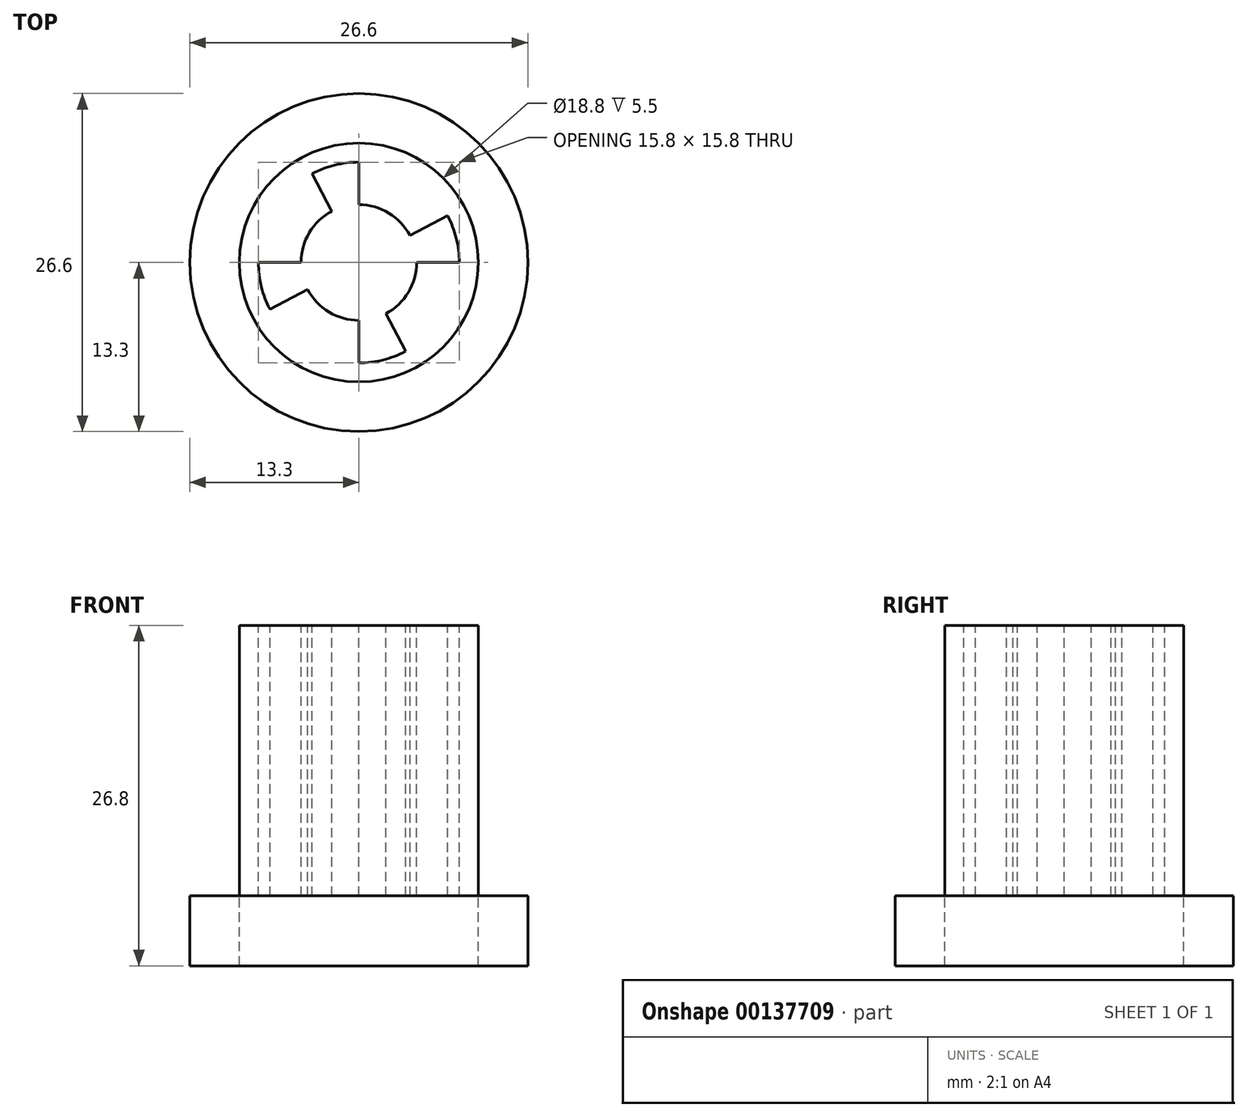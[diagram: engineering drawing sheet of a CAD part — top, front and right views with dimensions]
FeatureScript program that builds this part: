
annotation { "Feature Type Name" : "Feature", "Feature Type Description" : "" }
export const myFeature = defineFeature(function(context is Context, id is Id, definition is map)
    precondition{}
    {
        {
            var Q0;
            Q0=qCreatedBy(makeId("Top.planeOp"),FACE);
            var sketch = newSketch(context, id + "F0", { "sketchPlane" : qUnion([Q0])});
            skCircle(sketch, "E0", {"center": v(0, 0) * mm, "radius": 9.4 * mm});
            skCircle(sketch, "E1", {"center": v(0, 0) * mm, "radius": 13.3 * mm});
            skSolve(sketch);
        }
        {
            var Q0;
            Q0=makeQuery(id+"F0.imprint","IMPRINT",FACE,{"disambiguationData":[TD([[makeQuery(id+"F0.imprint","IMPRINT",EDGE,{"derivedFrom":sQuery(id+"F0.wireOp",EDGE,"E0")}),-1.0]])]});
            extrude(context, id + "F1", {"entities" : qUnion([Q0]), "oppositeDirection" : true, "depth" : 5.5 * mm});
        }
        {
            var Q0;
            Q0=qCreatedBy(makeId("Top.planeOp"),FACE);
            var sketch = newSketch(context, id + "F2", { "sketchPlane" : qUnion([Q0])});
            skCircle(sketch, "E2.0", {"center": v(0, 0) * mm, "radius": 9.4 * mm});
            skSolve(sketch);
        }
        {
            var Q0;
            Q0 = qSketchRegion(id + "F2", true);
            extrude(context, id + "F3", {"entities" : qUnion([Q0]), "depth" : 21.3 * mm});
        }
        {
            var Q0;
            Q0=qCreatedBy(makeId("Top.planeOp"),FACE);
            var sketch = newSketch(context, id + "F4", { "sketchPlane" : qUnion([Q0])});
            skCircle(sketch, "E3.0", {"center": v(0, 0) * mm, "radius": 7.9 * mm});
            skLineSegment(sketch, "E4", {"start": v(0, -4.55) * mm, "end": v(0, -7.9) * mm});
            skLineSegment(sketch, "E5", {"start": v(2.12, -4.02) * mm, "end": v(3.69, -6.99) * mm});
            skLineSegment(sketch, "E6", {"start": v(4.55, 0) * mm, "end": v(7.9, 0) * mm});
            skLineSegment(sketch, "E7", {"start": v(4.02, 2.12) * mm, "end": v(6.99, 3.69) * mm});
            skLineSegment(sketch, "E8", {"start": v(0, 4.55) * mm, "end": v(0, 7.9) * mm});
            skLineSegment(sketch, "E9", {"start": v(-2.12, 4.02) * mm, "end": v(-3.69, 6.99) * mm});
            skLineSegment(sketch, "E10", {"start": v(-4.02, -2.12) * mm, "end": v(-6.99, -3.69) * mm});
            skLineSegment(sketch, "E11", {"start": v(-4.55, 0) * mm, "end": v(-7.9, 0) * mm});
            skArc(sketch, "E12", {"start": v(2.12, -4.02) * mm, "mid": v(3.9, -2.35) * mm, "end": v(4.55, 0) * mm});
            skArc(sketch, "E13.trimOffspring", {"start": v(4.02, 2.12) * mm, "mid": v(2.35, 3.9) * mm, "end": v(0, 4.55) * mm});
            skArc(sketch, "E14.trimOffspring", {"start": v(-2.12, 4.02) * mm, "mid": v(-3.9, 2.35) * mm, "end": v(-4.55, 0) * mm});
            skPoint(sketch, "E15.trimOffspring.end.orphan", {"position": v(0, 7.9) * mm});
            skPoint(sketch, "E16.orphan", {"position": v(-3.69, 6.99) * mm});
            skArc(sketch, "E17.trimOffspring", {"start": v(-4.02, -2.12) * mm, "mid": v(-2.35, -3.9) * mm, "end": v(0, -4.55) * mm});
            skSolve(sketch);
        }
        {
            var Q0;
            Q0=makeQuery(id+"F3.opExtrude","CAP_FACE",FACE,{"disambiguationData":[OSD([sQuery(id+"F2.wireOp",EDGE,"E2.0")])],"isStart":false});
            var sketch = newSketch(context, id + "F5", { "sketchPlane" : qUnion([Q0])});
            skCircle(sketch, "E18.0", {"center": v(0, 0) * mm, "radius": 7.9 * mm});
            skLineSegment(sketch, "E18.1", {"start": v(-2.12, 4.02) * mm, "end": v(-3.69, 6.99) * mm});
            skArc(sketch, "E18.2", {"start": v(-2.12, 4.02) * mm, "mid": v(-3.9, 2.35) * mm, "end": v(-4.55, 0) * mm});
            skLineSegment(sketch, "E18.3", {"start": v(-4.55, 0) * mm, "end": v(-7.9, 0) * mm});
            skArc(sketch, "E18.4", {"start": v(-4.02, -2.12) * mm, "mid": v(-2.35, -3.9) * mm, "end": v(0, -4.55) * mm});
            skArc(sketch, "E18.5", {"start": v(2.12, -4.02) * mm, "mid": v(3.9, -2.35) * mm, "end": v(4.55, 0) * mm});
            skArc(sketch, "E18.6", {"start": v(4.02, 2.12) * mm, "mid": v(2.35, 3.9) * mm, "end": v(0, 4.55) * mm});
            skLineSegment(sketch, "E18.7", {"start": v(0, 4.55) * mm, "end": v(0, 7.9) * mm});
            skLineSegment(sketch, "E18.8", {"start": v(4.02, 2.12) * mm, "end": v(6.99, 3.69) * mm});
            skLineSegment(sketch, "E18.9", {"start": v(2.12, -4.02) * mm, "end": v(3.69, -6.99) * mm});
            skLineSegment(sketch, "E18.10", {"start": v(-4.02, -2.12) * mm, "end": v(-6.99, -3.69) * mm});
            skLineSegment(sketch, "E19.0", {"start": v(4.55, 0) * mm, "end": v(7.9, 0) * mm});
            skLineSegment(sketch, "E19.1", {"start": v(0, -4.55) * mm, "end": v(0, -7.9) * mm});
            skSolve(sketch);
        }
        {
            var Q0;
            {var subQ3=sQuery(id+"F5.wireOp",EDGE,"E18.1");Q0=makeQuery(id+"F5.imprint","IMPRINT",FACE,{"disambiguationData":[TD([[makeQuery(id+"F5.imprint","IMPRINT",EDGE,{"derivedFrom":subQ3}),-1.0]])]});}
            extrude(context, id + "F6", {"entities" : qUnion([Q0]), "operationType" : NewBodyOperationType.REMOVE, "oppositeDirection" : true, "depth" : 25 * mm});
        }
    });
